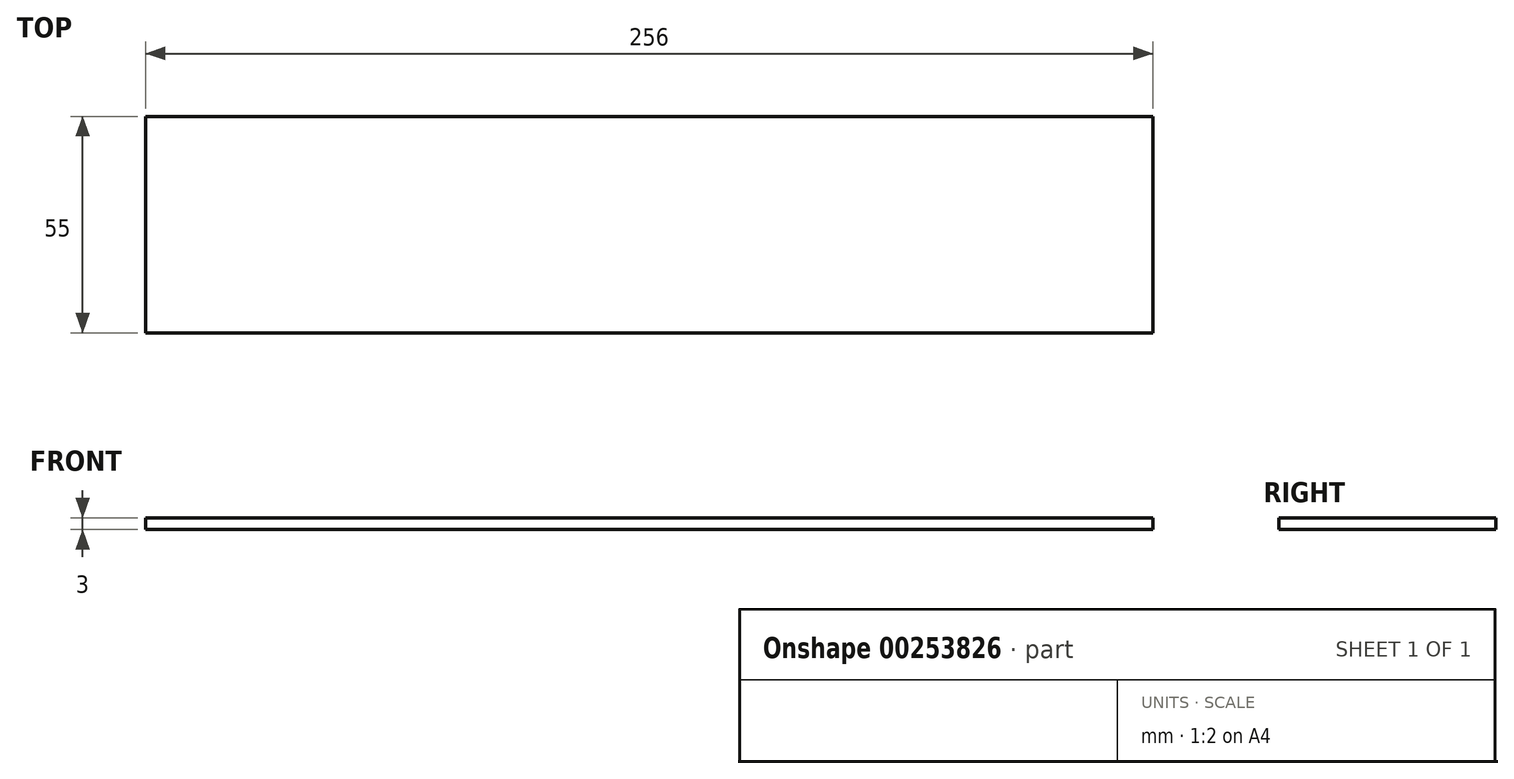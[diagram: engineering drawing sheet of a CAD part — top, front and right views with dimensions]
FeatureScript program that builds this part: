
annotation { "Feature Type Name" : "Feature", "Feature Type Description" : "" }
export const myFeature = defineFeature(function(context is Context, id is Id, definition is map)
    precondition{}
    {
        {
            var Q0;
            Q0=qCreatedBy(makeId("Top.planeOp"),FACE);
            var sketch = newSketch(context, id + "F0", { "sketchPlane" : qUnion([Q0])});
            skLineSegment(sketch, "E0", {"start": v(125, -27.5) * mm, "end": v(-125, -27.5) * mm});
            skLineSegment(sketch, "E1", {"start": v(-125, -27.5) * mm, "end": v(-125, 27.5) * mm});
            skLineSegment(sketch, "E2", {"start": v(-125, 27.5) * mm, "end": v(125, 27.5) * mm});
            skLineSegment(sketch, "E3", {"start": v(131, 27.5) * mm, "end": v(131, -27.5) * mm});
            skLineSegment(sketch, "E4", {"start": v(125, 27.5) * mm, "end": v(131, 27.5) * mm});
            skLineSegment(sketch, "E5", {"start": v(125, -27.5) * mm, "end": v(131, -27.5) * mm});
            skSolve(sketch);
        }
        {
            var Q0;
            Q0=makeQuery(id+"F0.imprint","IMPRINT",FACE,{"disambiguationData":[TD([[makeQuery(id+"F0.imprint","IMPRINT",EDGE,{"derivedFrom":sQuery(id+"F0.wireOp",EDGE,"E0")}),-1.0]])]});
            extrude(context, id + "F1", {"entities" : qUnion([Q0]), "depth" : 3 * mm});
        }
    });
